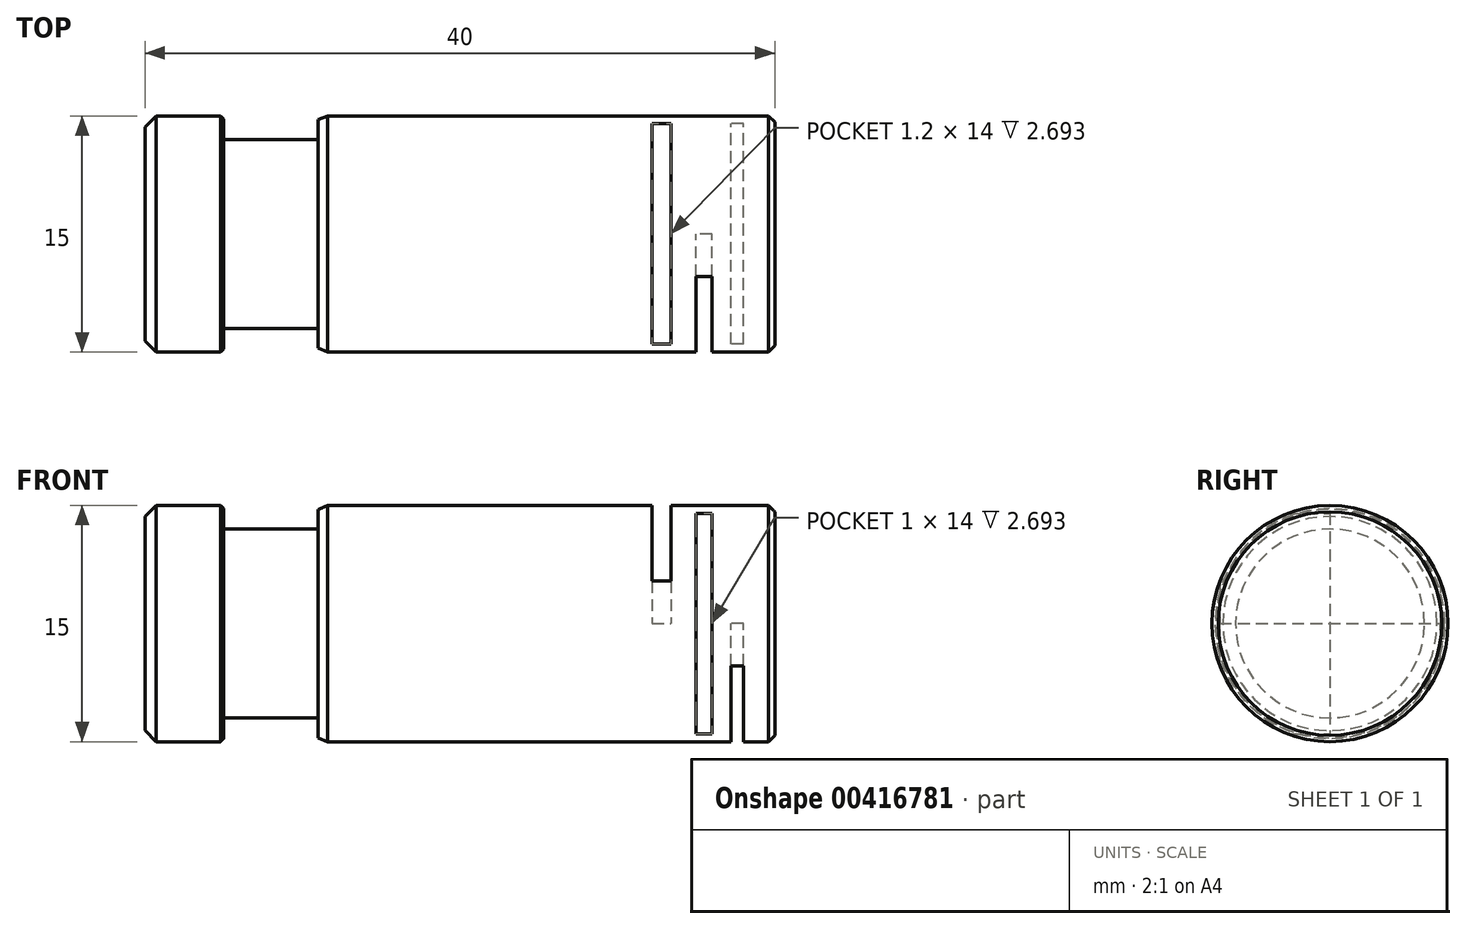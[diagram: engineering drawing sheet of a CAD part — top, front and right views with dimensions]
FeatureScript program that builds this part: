
annotation { "Feature Type Name" : "Feature", "Feature Type Description" : "" }
export const myFeature = defineFeature(function(context is Context, id is Id, definition is map)
    precondition{}
    {
        {
            var Q0;
            Q0=qCreatedBy(makeId("Front.planeOp"),FACE);
            var sketch = newSketch(context, id + "F0", { "sketchPlane" : qUnion([Q0])});
            skLineSegment(sketch, "E0.bottom", {"start": v(0, 0) * mm, "end": v(40, 0) * mm});
            skLineSegment(sketch, "E0.top", {"start": v(0, 7.5) * mm, "end": v(40, 7.5) * mm});
            skLineSegment(sketch, "E0.left", {"start": v(0, 0) * mm, "end": v(0, 7.5) * mm});
            skLineSegment(sketch, "E0.right", {"start": v(40, 0) * mm, "end": v(40, 7.5) * mm});
            skLineSegment(sketch, "E1", {"start": v(5, 7.5) * mm, "end": v(5, 6) * mm});
            skLineSegment(sketch, "E2", {"start": v(5, 6) * mm, "end": v(11, 6) * mm});
            skLineSegment(sketch, "E3", {"start": v(11, 6) * mm, "end": v(11, 7.5) * mm});
            skLineSegment(sketch, "E4", {"start": v(11, 7.5) * mm, "end": v(5, 7.5) * mm});
            skSolve(sketch);
        }
        {
            var Q0;
            Q0=makeQuery(id+"F0.imprint","IMPRINT",FACE,{"disambiguationData":[TD([[makeQuery(id+"F0.imprint","IMPRINT",EDGE,{"derivedFrom":sQuery(id+"F0.wireOp",EDGE,"E0.bottom")}),1.0]])]});
            var Q1;
            Q1=sQuery(id+"F0.wireOp",EDGE,"E0.bottom");
            revolve(context, id + "F1", {"entities" : qUnion([Q0]), "axis" : qUnion([Q1]), "revolveType" : RevolveType.FULL});
        }
        {
            var Q0;
            Q0=makeQuery(id+"F1.opRevolve","SWEPT_EDGE",EDGE,{"disambiguationData":[OSD([sQuery(id+"F0.wireOp",EDGE,"E0.top"),sQuery(id+"F0.wireOp",EDGE,"E0.left")])]});
            chamfer(context, id + "F2", {"entities" : qUnion([Q0]), "width" : .7 * mm, "tangentPropagation" : true});
        }
        {
            var Q0;
            Q0=makeQuery(id+"F1.opRevolve","SWEPT_EDGE",EDGE,{"disambiguationData":[OSD([sQuery(id+"F0.wireOp",EDGE,"E0.top"),sQuery(id+"F0.wireOp",EDGE,"E1"),sQuery(id+"F0.wireOp",EDGE,"E4")])]});
            var Q1;
            Q1=makeQuery(id+"F1.opRevolve","SWEPT_EDGE",EDGE,{"disambiguationData":[OSD([sQuery(id+"F0.wireOp",EDGE,"E0.top"),sQuery(id+"F0.wireOp",EDGE,"E3"),sQuery(id+"F0.wireOp",EDGE,"E4")])]});
            chamfer(context, id + "F3", {"entities" : qUnion([Q0, Q1]), "width" : .2 * mm, "tangentPropagation" : true});
        }
        {
            var Q0;
            Q0=qCreatedBy(makeId("Front.planeOp"),FACE);
            var sketch = newSketch(context, id + "F4", { "sketchPlane" : qUnion([Q0])});
            skLineSegment(sketch, "E5.bottom", {"start": v(36, 7) * mm, "end": v(35, 7) * mm});
            skLineSegment(sketch, "E5.top", {"start": v(36, -7) * mm, "end": v(35, -7) * mm});
            skLineSegment(sketch, "E5.left", {"start": v(36, 7) * mm, "end": v(36, -7) * mm});
            skLineSegment(sketch, "E5.right", {"start": v(35, 7) * mm, "end": v(35, -7) * mm});
            skPoint(sketch, "E5.middle", {"position": v(35.5, 0) * mm});
            skSolve(sketch);
        }
        {
            var Q0;
            {var subQ0=sQuery(id+"F0.wireOp",EDGE,"E0.top");Q0=makeQuery(id+"F1.opRevolve","SWEPT_FACE",FACE,{"disambiguationData":[OSD([subQ0]),TDD([makeQuery(id+"F0.imprint","IMPRINT",EDGE,{"disambiguationData":[TD([[makeQuery(id+"F0.imprint","INTERSECT",VERTEX,{"derivedFrom":[subQ0,sQuery(id+"F0.wireOp",EDGE,"E0.right")]}),1.0]])],"derivedFrom":subQ0})])]});}
            chamfer(context, id + "F5", {"entities" : qUnion([Q0]), "width" : .4 * mm, "tangentPropagation" : true});
        }
        {
            var Q0;
            Q0 = qSketchRegion(id + "F4", true);
            extrude(context, id + "F6", {"entities" : qUnion([Q0]), "operationType" : NewBodyOperationType.REMOVE, "depth" : 7.5 * mm});
        }
        {
            var Q0;
            Q0=qCreatedBy(makeId("Top.planeOp"),FACE);
            var sketch = newSketch(context, id + "F7", { "sketchPlane" : qUnion([Q0])});
            skLineSegment(sketch, "E6.bottom", {"start": v(32.2, -7) * mm, "end": v(33.4, -7) * mm});
            skLineSegment(sketch, "E6.top", {"start": v(32.2, 7) * mm, "end": v(33.4, 7) * mm});
            skLineSegment(sketch, "E6.left", {"start": v(32.2, -7) * mm, "end": v(32.2, 7) * mm});
            skLineSegment(sketch, "E6.right", {"start": v(33.4, -7) * mm, "end": v(33.4, 7) * mm});
            skPoint(sketch, "E6.middle", {"position": v(32.8, 0) * mm});
            skSolve(sketch);
        }
        {
            var Q0;
            Q0 = qSketchRegion(id + "F7", true);
            extrude(context, id + "F8", {"entities" : qUnion([Q0]), "operationType" : NewBodyOperationType.REMOVE, "depth" : 7.5 * mm});
        }
        {
            var Q0;
            Q0=qCreatedBy(makeId("Top.planeOp"),FACE);
            var sketch = newSketch(context, id + "F9", { "sketchPlane" : qUnion([Q0])});
            skLineSegment(sketch, "E7.bottom", {"start": v(38, -7) * mm, "end": v(37.2, -7) * mm});
            skLineSegment(sketch, "E7.top", {"start": v(38, 7) * mm, "end": v(37.2, 7) * mm});
            skLineSegment(sketch, "E7.left", {"start": v(38, -7) * mm, "end": v(38, 7) * mm});
            skLineSegment(sketch, "E7.right", {"start": v(37.2, -7) * mm, "end": v(37.2, 7) * mm});
            skPoint(sketch, "E7.middle", {"position": v(37.6, 0) * mm});
            skSolve(sketch);
        }
        {
            var Q0;
            Q0 = qSketchRegion(id + "F9", true);
            extrude(context, id + "F10", {"entities" : qUnion([Q0]), "operationType" : NewBodyOperationType.REMOVE, "oppositeDirection" : true, "depth" : 7.5 * mm});
        }
    });
